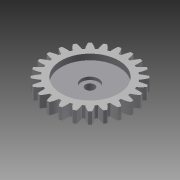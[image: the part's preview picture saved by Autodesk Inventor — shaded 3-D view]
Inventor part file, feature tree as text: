
AUTODESK INVENTOR PART (.ipt)
format: ipt  version: 2014 (Build 180170000, 170)  size: 297,472 bytes
history: native  units: mm
features: extrude x6, sketch x6, other x4, projected_geometry x1
ambient origin geometry x8: Origin, YZ Plane, XZ Plane, XY Plane, X Axis, Y Axis, Z Axis, Center Point
bodies: Body1 (feature_tree)
feature tree (17):
  other  "平歯車1"
  extrude  "押し出し1"  Depth=10.0mm
  extrude  "押し出し2"  Depth=12.0mm
  extrude  "押し出し3"  Depth=3.8mm TaperAngle=0.0deg
  extrude  "押し出し4"  Depth=20.0mm
  extrude  "押し出し5"  Depth=0.5mm TaperAngle=0.0deg
  extrude  "押し出し7"  Depth=4.0mm TaperAngle=0.0deg
  other  "Solid1::平歯車1"
  other  "TaggingFeature1"
  sketch  "スケッチ1"
  sketch  "スケッチ2"
  sketch  "スケッチ3"
  sketch  "スケッチ4"
  sketch  "スケッチ5"
  projected_geometry  "投影ループ1"
  sketch  "スケッチ7"
  other  "ソリッド1"
